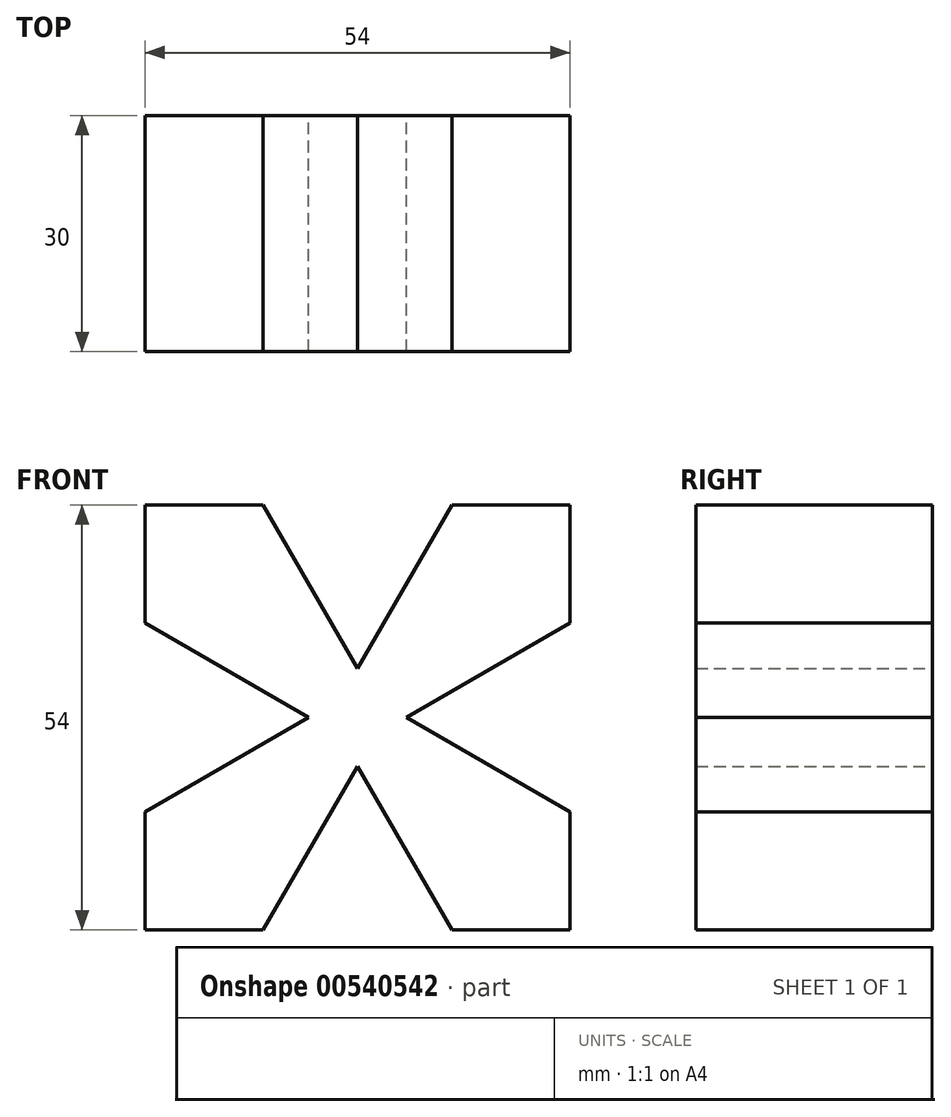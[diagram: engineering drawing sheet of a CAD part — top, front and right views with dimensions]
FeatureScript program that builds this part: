
annotation { "Feature Type Name" : "Feature", "Feature Type Description" : "" }
export const myFeature = defineFeature(function(context is Context, id is Id, definition is map)
    precondition{}
    {
        {
            var Q0;
            Q0=qCreatedBy(makeId("Front.planeOp"),FACE);
            var sketch = newSketch(context, id + "F0", { "sketchPlane" : qUnion([Q0])});
            skLineSegment(sketch, "E0", {"start": v(0, 6.22) * mm, "end": v(-12, 27) * mm});
            skLineSegment(sketch, "E1", {"start": v(-12, 27) * mm, "end": v(-27, 27) * mm});
            skLineSegment(sketch, "E2", {"start": v(-27, 27) * mm, "end": v(-27, 12) * mm});
            skLineSegment(sketch, "E3", {"start": v(-27, 12) * mm, "end": v(-6.22, 0) * mm});
            skLineSegment(sketch, "E4", {"start": v(-6.22, 0) * mm, "end": v(-27, -12) * mm});
            skLineSegment(sketch, "E5", {"start": v(-27, -12) * mm, "end": v(-27, -27) * mm});
            skLineSegment(sketch, "E6", {"start": v(-27, -27) * mm, "end": v(-12, -27) * mm});
            skLineSegment(sketch, "E7", {"start": v(0, -6.22) * mm, "end": v(12, -27) * mm});
            skLineSegment(sketch, "E8", {"start": v(6.22, 0) * mm, "end": v(27, 12) * mm});
            skLineSegment(sketch, "E9", {"start": v(27, 27) * mm, "end": v(12, 27) * mm});
            skLineSegment(sketch, "E10", {"start": v(12, 27) * mm, "end": v(0, 6.22) * mm});
            skLineSegment(sketch, "E11", {"start": v(-12, -27) * mm, "end": v(0, -6.22) * mm});
            skLineSegment(sketch, "E12", {"start": v(12, -27) * mm, "end": v(27, -27) * mm});
            skLineSegment(sketch, "E13", {"start": v(27, -27) * mm, "end": v(27, -12) * mm});
            skLineSegment(sketch, "E14", {"start": v(27, 27) * mm, "end": v(27, 12) * mm});
            skLineSegment(sketch, "E15", {"start": v(6.22, 0) * mm, "end": v(27, -12) * mm});
            skSolve(sketch);
        }
        {
            var Q0;
            Q0=makeQuery(id+"F0.imprint","IMPRINT",FACE,{"disambiguationData":[TD([[makeQuery(id+"F0.imprint","IMPRINT",EDGE,{"derivedFrom":sQuery(id+"F0.wireOp",EDGE,"E0")}),1.0]])]});
            extrude(context, id + "F1", {"entities" : qUnion([Q0]), "depth" : 30 * mm, "offsetDistance" : 25 * mm});
        }
    });
